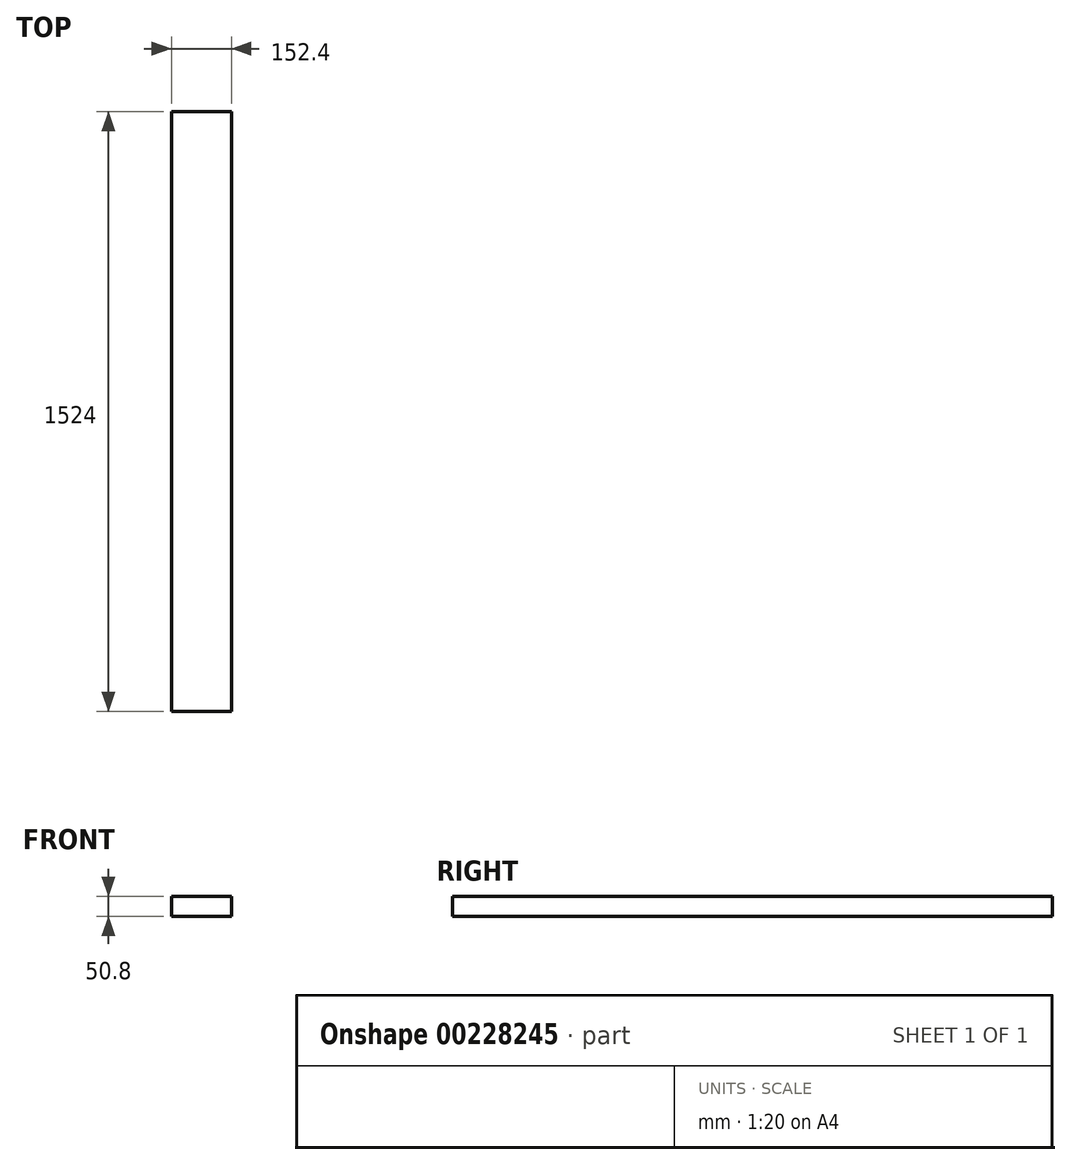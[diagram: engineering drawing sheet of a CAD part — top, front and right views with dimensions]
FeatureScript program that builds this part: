
annotation { "Feature Type Name" : "Feature", "Feature Type Description" : "" }
export const myFeature = defineFeature(function(context is Context, id is Id, definition is map)
    precondition{}
    {
        {
            var Q0;
            Q0=qCreatedBy(makeId("Front.planeOp"),FACE);
            var sketch = newSketch(context, id + "F0", { "sketchPlane" : qUnion([Q0])});
            skLineSegment(sketch, "E0.bottom", {"start": v(-67.44, 10.6) * mm, "end": v(84.96, 10.6) * mm});
            skLineSegment(sketch, "E0.top", {"start": v(-67.44, -40.2) * mm, "end": v(84.96, -40.2) * mm});
            skLineSegment(sketch, "E0.left", {"start": v(-67.44, 10.6) * mm, "end": v(-67.44, -40.2) * mm});
            skLineSegment(sketch, "E0.right", {"start": v(84.96, 10.6) * mm, "end": v(84.96, -40.2) * mm});
            skSolve(sketch);
        }
        {
            var Q0;
            Q0 = qSketchRegion(id + "F0", true);
            extrude(context, id + "F1", {"entities" : qUnion([Q0]), "depth" : 1524 * mm});
        }
    });
